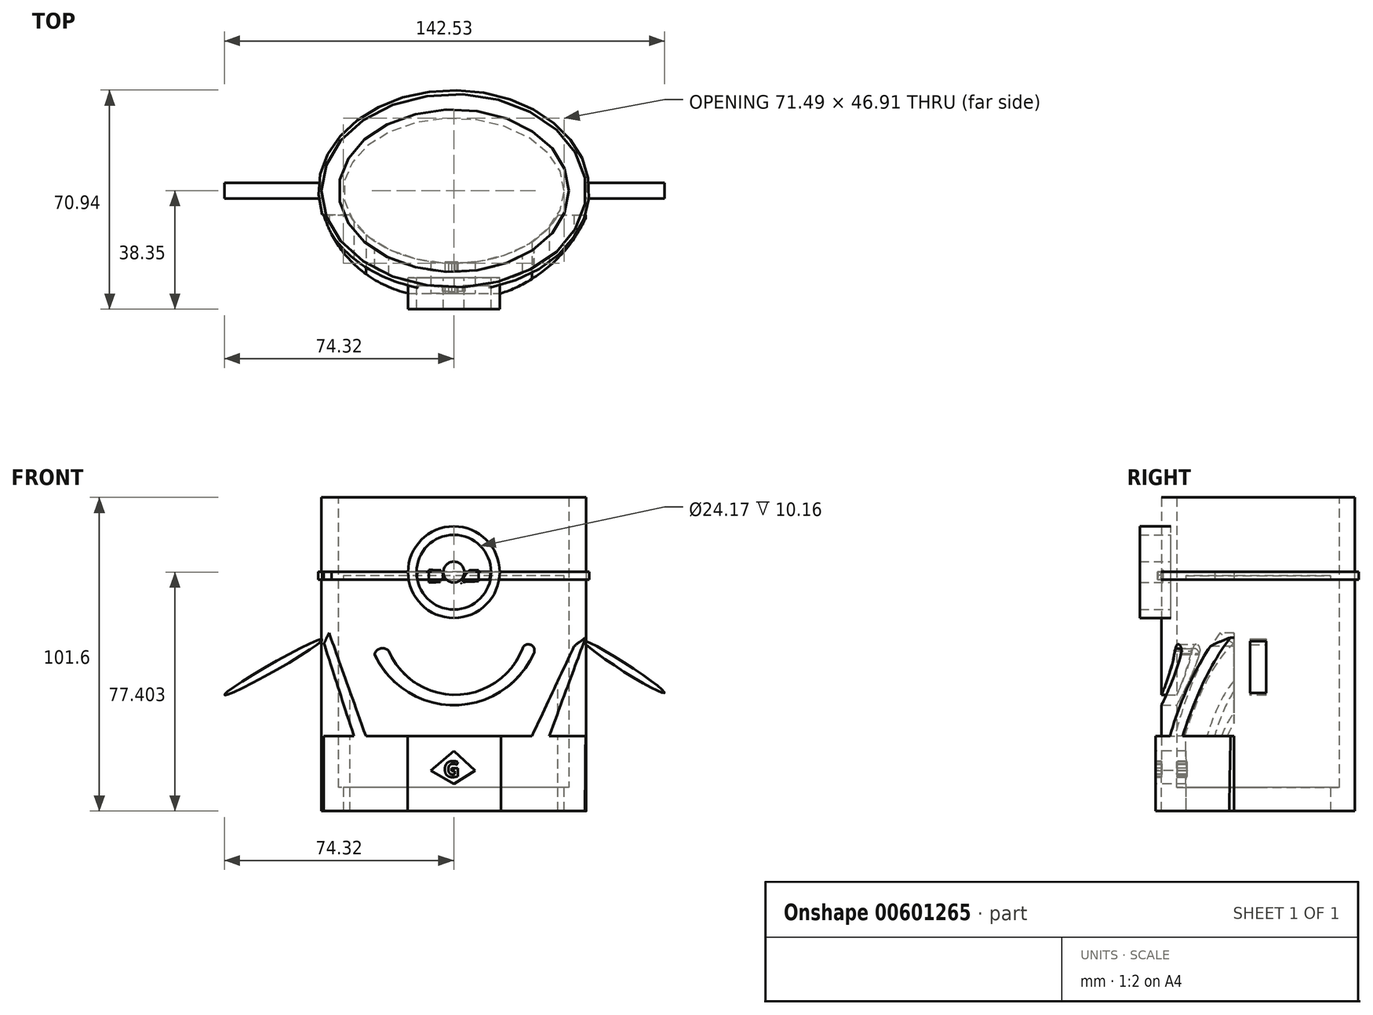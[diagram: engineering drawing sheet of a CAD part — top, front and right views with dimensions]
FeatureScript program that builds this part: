
annotation { "Feature Type Name" : "Feature", "Feature Type Description" : "" }
export const myFeature = defineFeature(function(context is Context, id is Id, definition is map)
    precondition{}
    {
        {
            var Q0;
            Q0=qCreatedBy(makeId("Top.planeOp"),FACE);
            var sketch = newSketch(context, id + "F0", { "sketchPlane" : qUnion([Q0])});
            skEllipse(sketch, "E0", {"center": v(0, 0) * mm, "majorRadius": 42.87 * mm, "minorRadius": 31.3 * mm, "majorAxis": v(-1, 0)});
            skEllipse(sketch, "E1", {"center": v(0, 0) * mm, "majorRadius": 37.27 * mm, "minorRadius": 26.31 * mm, "majorAxis": v(1, 0)});
            skSolve(sketch);
        }
        {
            var Q0;
            Q0=makeQuery(id+"F0.imprint","IMPRINT",FACE,{"disambiguationData":[TD([[makeQuery(id+"F0.imprint","IMPRINT",EDGE,{"derivedFrom":sQuery(id+"F0.wireOp",EDGE,"E0")}),1.0]])]});
            extrude(context, id + "F1", {"entities" : qUnion([Q0]), "depth" : 101.6 * mm, "offsetDistance" : 25.4 * mm});
        }
        {
            var Q0;
            Q0=qCreatedBy(makeId("Front.planeOp"),FACE);
            cPlane(context, id + "F2", {"entities" : qUnion([Q0]), "cplaneType" : CPlaneType.OFFSET, "offset" : 28.2 * mm, "width" : 152.4 * mm, "height" : 152.4 * mm});
        }
        {
            var Q0;
            Q0=qCreatedBy(id+"F2.planeOp",FACE);
            var sketch = newSketch(context, id + "F3", { "sketchPlane" : qUnion([Q0])});
            skCircle(sketch, "E2", {"center": v(0, 77.4) * mm, "radius": 14.84 * mm});
            skCircle(sketch, "E3", {"center": v(0, 77.4) * mm, "radius": 12.08 * mm});
            skCircle(sketch, "E4", {"center": v(0, 77.4) * mm, "radius": 3.38 * mm});
            skSolve(sketch);
        }
        {
            var Q0;
            Q0=makeQuery(id+"F3.imprint","IMPRINT",FACE,{"disambiguationData":[TD([[makeQuery(id+"F3.imprint","IMPRINT",EDGE,{"derivedFrom":sQuery(id+"F3.wireOp",EDGE,"E2")}),1.0]])]});
            extrude(context, id + "F4", {"entities" : qUnion([Q0]), "depth" : 10.16 * mm, "offsetDistance" : 25.4 * mm});
        }
        {
            var Q0;
            Q0=makeQuery(id+"F3.imprint","IMPRINT",FACE,{"disambiguationData":[TD([[makeQuery(id+"F3.imprint","IMPRINT",EDGE,{"derivedFrom":sQuery(id+"F3.wireOp",EDGE,"E4")}),1.0]])]});
            extrude(context, id + "F5", {"entities" : qUnion([Q0]), "depth" : 10.16 * mm, "offsetDistance" : 25.4 * mm});
        }
        {
            var Q0;
            Q0=qCreatedBy(makeId("Top.planeOp"),FACE);
            cPlane(context, id + "F6", {"entities" : qUnion([Q0]), "cplaneType" : CPlaneType.OFFSET, "offset" : 76.2 * mm, "width" : 152.4 * mm, "height" : 152.4 * mm});
        }
        {
            var Q0;
            Q0=qCreatedBy(id+"F6.planeOp",FACE);
            var sketch = newSketch(context, id + "F7", { "sketchPlane" : qUnion([Q0])});
            skEllipse(sketch, "E5", {"center": v(0, 0) * mm, "majorRadius": 43.86 * mm, "minorRadius": 32.59 * mm, "majorAxis": v(-1, 0)});
            skFitSpline(sketch, "E6.0", {"points": [v(-42.3, 1.52) * mm, v(-42.36, 0) * mm, v(-42.3, -1.52) * mm, v(-42.1, -3.52) * mm, v(-41.6, -6) * mm, v(-40.62, -8.91) * mm, v(-39.26, -11.74) * mm, v(-37.52, -14.48) * mm, v(-35.42, -17.08) * mm, v(-33.37, -19.14) * mm, v(-31.56, -20.7) * mm, v(-30.12, -21.83) * mm, v(-28.6, -22.9) * mm, v(-26.49, -24.25) * mm, v(-23.7, -25.79) * mm, v(-20.12, -27.37) * mm, v(-16.36, -28.7) * mm, v(-12.44, -29.74) * mm, v(-8.4, -30.5) * mm, v(-4.93, -30.88) * mm, v(-2.12, -31.04) * mm, v(0, -31.07) * mm, v(2.12, -31.04) * mm, v(4.93, -30.88) * mm, v(8.4, -30.5) * mm, v(12.44, -29.74) * mm, v(16.36, -28.7) * mm, v(20.12, -27.37) * mm, v(23.7, -25.79) * mm, v(26.49, -24.25) * mm, v(28.6, -22.9) * mm, v(30.12, -21.83) * mm, v(31.56, -20.7) * mm, v(33.37, -19.14) * mm, v(35.42, -17.08) * mm, v(37.52, -14.48) * mm, v(39.26, -11.74) * mm, v(40.62, -8.91) * mm, v(41.6, -6) * mm, v(42.1, -3.52) * mm, v(42.3, -1.52) * mm, v(42.36, 0) * mm, v(42.3, 1.52) * mm, v(42.1, 3.52) * mm, v(41.6, 6) * mm, v(40.62, 8.91) * mm, v(39.26, 11.74) * mm, v(37.52, 14.48) * mm, v(35.42, 17.08) * mm, v(33.37, 19.14) * mm, v(31.56, 20.7) * mm, v(30.12, 21.83) * mm, v(28.6, 22.9) * mm, v(26.49, 24.25) * mm, v(23.7, 25.79) * mm, v(20.12, 27.37) * mm, v(16.36, 28.7) * mm, v(12.44, 29.74) * mm, v(8.4, 30.5) * mm, v(4.93, 30.88) * mm, v(2.12, 31.04) * mm, v(0, 31.07) * mm, v(-2.12, 31.04) * mm, v(-4.93, 30.88) * mm, v(-8.4, 30.5) * mm, v(-12.44, 29.74) * mm, v(-16.36, 28.7) * mm, v(-20.12, 27.37) * mm, v(-23.7, 25.79) * mm, v(-26.49, 24.25) * mm, v(-28.6, 22.9) * mm, v(-30.12, 21.83) * mm, v(-31.56, 20.7) * mm, v(-33.37, 19.14) * mm, v(-35.42, 17.08) * mm, v(-37.52, 14.48) * mm, v(-39.26, 11.74) * mm, v(-40.62, 8.91) * mm, v(-41.6, 6) * mm, v(-42.1, 3.52) * mm, v(-42.3, 1.52) * mm, v(-42.36, 0) * mm, v(-42.3, -1.52) * mm, v(-42.3, 1.52) * mm]});
            skSolve(sketch);
        }
        {
            var Q0;
            Q0=makeQuery(id+"F7.imprint","IMPRINT",FACE,{"disambiguationData":[TD([[makeQuery(id+"F7.imprint","IMPRINT",EDGE,{"derivedFrom":sQuery(id+"F7.wireOp",EDGE,"E5")}),1.0]])]});
            extrude(context, id + "F8", {"entities" : qUnion([Q0]), "endBound" : BoundingType.SYMMETRIC, "depth" : 2.54 * mm, "offsetDistance" : 25.4 * mm});
        }
        {
            var Q0;
            Q0=qCreatedBy(makeId("Top.planeOp"),FACE);
            var sketch = newSketch(context, id + "F9", { "sketchPlane" : qUnion([Q0])});
            skEllipse(sketch, "E7", {"center": v(0, 0) * mm, "majorRadius": 39.81 * mm, "minorRadius": 29.81 * mm, "majorAxis": v(1, 0)});
            skSolve(sketch);
        }
        {
            var Q0;
            Q0=makeQuery(id+"F9.imprint","IMPRINT",FACE,{"disambiguationData":[TD([[makeQuery(id+"F9.imprint","IMPRINT",EDGE,{"derivedFrom":sQuery(id+"F9.wireOp",EDGE,"E7")}),1.0]])]});
            var Q1;
            Q1=sQuery(id+"F9.wireOp",EDGE,"E7");
            extrude(context, id + "F10", {"entities" : qUnion([Q0]), "operationType" : NewBodyOperationType.ADD, "surfaceEntities" : qUnion([Q1]), "depth" : 7.62 * mm, "offsetDistance" : 25.4 * mm});
        }
        {
            var Q0;
            Q0=qCreatedBy(id+"F2.planeOp",FACE);
            var sketch = newSketch(context, id + "F11", { "sketchPlane" : qUnion([Q0])});
            skArc(sketch, "E8", {"start": v(-25.68, 50.76) * mm, "mid": v(0.23, 34.33) * mm, "end": v(25.9, 51.15) * mm});
            skArc(sketch, "E9", {"start": v(-21.06, 51.92) * mm, "mid": v(0.85, 37.67) * mm, "end": v(22.24, 52.68) * mm});
            skArc(sketch, "E10", {"start": v(-21.06, 51.92) * mm, "mid": v(-23.71, 52.7) * mm, "end": v(-25.68, 50.76) * mm});
            skArc(sketch, "E11", {"start": v(25.9, 51.15) * mm, "mid": v(24.9, 53.89) * mm, "end": v(22.24, 52.68) * mm});
            skSolve(sketch);
        }
        {
            var Q0;
            Q0=makeQuery(id+"F11.imprint","IMPRINT",FACE,{"disambiguationData":[TD([[makeQuery(id+"F11.imprint","IMPRINT",EDGE,{"derivedFrom":sQuery(id+"F11.wireOp",EDGE,"E8")}),1.0]])]});
            var Q1;
            Q1=sQuery(id+"F11.wireOp",EDGE,"E9");
            var Q2;
            Q2=sQuery(id+"F11.wireOp",EDGE,"E8");
            var Q3;
            Q3=sQuery(id+"F11.wireOp",EDGE,"E10");
            var Q4;
            Q4=sQuery(id+"F11.wireOp",EDGE,"E11");
            extrude(context, id + "F12", {"entities" : qUnion([Q0]), "operationType" : NewBodyOperationType.REMOVE, "surfaceEntities" : qUnion([Q1, Q2, Q3, Q4]), "endBound" : BoundingType.SYMMETRIC, "depth" : 25.4 * mm, "offsetDistance" : 25.4 * mm});
        }
        {
            var Q0;
            Q0=qCreatedBy(makeId("Front.planeOp"),FACE);
            var sketch = newSketch(context, id + "F13", { "sketchPlane" : qUnion([Q0])});
            skEllipse(sketch, "E12", {"center": v(-58.26, 46.72) * mm, "majorRadius": 18.47 * mm, "minorRadius": 1.24 * mm, "majorAxis": v(0.87, 0.5)});
            skEllipse(sketch, "E13", {"center": v(55.02, 46.72) * mm, "majorRadius": 15.64 * mm, "minorRadius": 1.25 * mm, "majorAxis": v(-0.84, 0.54)});
            skSolve(sketch);
        }
        {
            var Q0;
            Q0 = qSketchRegion(id + "F13", true);
            extrude(context, id + "F14", {"entities" : qUnion([Q0]), "operationType" : NewBodyOperationType.ADD, "endBound" : BoundingType.SYMMETRIC, "depth" : 5.08 * mm, "offsetDistance" : 25.4 * mm});
        }
        {
            var Q0;
            Q0=qCreatedBy(id+"F2.planeOp",FACE);
            cPlane(context, id + "F15", {"entities" : qUnion([Q0]), "cplaneType" : CPlaneType.OFFSET, "offset" : 5.08 * mm, "width" : 152.4 * mm, "height" : 152.4 * mm});
        }
        {
            var Q0;
            Q0=qCreatedBy(id+"F15.planeOp",FACE);
            var sketch = newSketch(context, id + "F16", { "sketchPlane" : qUnion([Q0])});
            skLineSegment(sketch, "E14", {"start": v(-28.48, 24.29) * mm, "end": v(25.3, 24.29) * mm});
            skLineSegment(sketch, "E15", {"start": v(25.3, 24.29) * mm, "end": v(38.93, 53.42) * mm});
            skLineSegment(sketch, "E16", {"start": v(38.93, 53.42) * mm, "end": v(42.65, 56.21) * mm});
            skLineSegment(sketch, "E17", {"start": v(42.65, 56.21) * mm, "end": v(30.88, 24.29) * mm});
            skLineSegment(sketch, "E18", {"start": v(30.88, 24.29) * mm, "end": v(42.65, 24.29) * mm});
            skLineSegment(sketch, "E19", {"start": v(42.65, 24.29) * mm, "end": v(30.88, 24.29) * mm});
            skLineSegment(sketch, "E20", {"start": v(-28.48, 24.29) * mm, "end": v(-40.41, 57.76) * mm});
            skLineSegment(sketch, "E21", {"start": v(-40.41, 57.76) * mm, "end": v(-42.05, 54.27) * mm});
            skLineSegment(sketch, "E22", {"start": v(-42.05, 54.27) * mm, "end": v(-32.35, 24.29) * mm});
            skLineSegment(sketch, "E23", {"start": v(-32.35, 24.29) * mm, "end": v(-43.2, 24.29) * mm});
            skLineSegment(sketch, "E24", {"start": v(-7.4, 13.13) * mm, "end": v(0, 19.48) * mm});
            skLineSegment(sketch, "E25", {"start": v(0, 19.48) * mm, "end": v(6.85, 13.13) * mm});
            skLineSegment(sketch, "E26", {"start": v(6.85, 13.13) * mm, "end": v(0, 8.79) * mm});
            skLineSegment(sketch, "E27", {"start": v(0, 8.79) * mm, "end": v(-7.4, 13.13) * mm});
            skLineSegment(sketch, "E28", {"start": v(-43.2, 24.29) * mm, "end": v(-42.23, 0) * mm});
            skLineSegment(sketch, "E29", {"start": v(-42.23, 0) * mm, "end": v(42.45, 0) * mm});
            skLineSegment(sketch, "E30", {"start": v(42.45, 0) * mm, "end": v(42.65, 24.29) * mm});
            skLineSegment(sketch, "E31.trimOffspring", {"start": v(25.3, 24.29) * mm, "end": v(-28.48, 24.29) * mm});
            skSolve(sketch);
        }
        {
            var Q0;
            Q0=makeQuery(id+"F16.imprint","IMPRINT",FACE,{"disambiguationData":[TD([[makeQuery(id+"F16.imprint","IMPRINT",EDGE,{"derivedFrom":sQuery(id+"F16.wireOp",EDGE,"E15")}),-1.0]])]});
            var Q1;
            Q1=makeQuery(id+"F1.opExtrude","SWEPT_FACE",FACE,{"disambiguationData":[OSD([sQuery(id+"F0.wireOp",EDGE,"E0")])]});
            extrude(context, id + "F17", {"entities" : qUnion([Q0]), "oppositeDirection" : true, "depth" : 25.4 * mm, "endBoundEntityFace" : qUnion([Q1]), "offsetDistance" : 25.4 * mm});
        }
        {
            var Q0;
            Q0=qCreatedBy(id+"F6.planeOp",FACE);
            var sketch = newSketch(context, id + "F18", { "sketchPlane" : qUnion([Q0])});
            skEllipse(sketch, "E32", {"center": v(0, 0) * mm, "majorRadius": 35.74 * mm, "minorRadius": 23.45 * mm, "majorAxis": v(1, 0)});
            skSolve(sketch);
        }
        {
            var Q0;
            Q0=makeQuery(id+"F18.imprint","IMPRINT",FACE,{"disambiguationData":[TD([[makeQuery(id+"F18.imprint","IMPRINT",EDGE,{"derivedFrom":sQuery(id+"F18.wireOp",EDGE,"E32")}),1.0]])]});
            var Q1;
            Q1=sQuery(id+"F18.wireOp",EDGE,"E32");
            extrude(context, id + "F19", {"entities" : qUnion([Q0]), "operationType" : NewBodyOperationType.REMOVE, "surfaceEntities" : qUnion([Q1]), "oppositeDirection" : true, "depth" : 76.2 * mm, "offsetDistance" : 25.4 * mm});
        }
        {
            var Q0;
            Q0=makeQuery(id+"F17.opExtrude","CAP_FACE",FACE,{"disambiguationData":[OSD([sQuery(id+"F16.wireOp",EDGE,"E15"),sQuery(id+"F16.wireOp",EDGE,"E16"),sQuery(id+"F16.wireOp",EDGE,"E17"),sQuery(id+"F16.wireOp",EDGE,"E19"),sQuery(id+"F16.wireOp",EDGE,"E20"),sQuery(id+"F16.wireOp",EDGE,"E21"),sQuery(id+"F16.wireOp",EDGE,"E22"),sQuery(id+"F16.wireOp",EDGE,"E23"),sQuery(id+"F16.wireOp",EDGE,"E24"),sQuery(id+"F16.wireOp",EDGE,"E25"),sQuery(id+"F16.wireOp",EDGE,"E26"),sQuery(id+"F16.wireOp",EDGE,"E27"),sQuery(id+"F16.wireOp",EDGE,"E28"),sQuery(id+"F16.wireOp",EDGE,"E29"),sQuery(id+"F16.wireOp",EDGE,"E30"),sQuery(id+"F16.wireOp",EDGE,"E31.trimOffspring")])],"isStart":true});
            var sketch = newSketch(context, id + "F20", { "sketchPlane" : qUnion([Q0])});
            skText(sketch, "E33", { "text": "G", "fontName": "OpenSans-Bold.ttf"});
            const initialGuessF20  = {"E33": [-0.00332, 0.01106, 1, 0, 0.00515]};
            skSetInitialGuess(sketch, initialGuessF20);
            skSolve(sketch);
        }
        {
            var Q0;
            Q0=makeQuery(id+"F20.imprint","IMPRINT",FACE,{"disambiguationData":[TD([[makeQuery(id+"F20.imprint","IMPRINT",EDGE,{"derivedFrom":sQuery(id+"F20.wireOp",EDGE,"E33.sketch_text.stroke-0")}),-1.0]])]});
            extrude(context, id + "F21", {"entities" : qUnion([Q0]), "operationType" : NewBodyOperationType.ADD, "oppositeDirection" : true, "depth" : 10.16 * mm, "offsetDistance" : 25.4 * mm});
        }
        {
            var Q0;
            Q0=qCreatedBy(id+"F15.planeOp",FACE);
            var sketch = newSketch(context, id + "F22", { "sketchPlane" : qUnion([Q0])});
            skLineSegment(sketch, "E34", {"start": v(-4.25, 78.4) * mm, "end": v(-2.49, 73.77) * mm});
            skLineSegment(sketch, "E35", {"start": v(-2.49, 73.77) * mm, "end": v(-11.02, 73.77) * mm});
            skLineSegment(sketch, "E36", {"start": v(-11.02, 73.77) * mm, "end": v(-11.67, 77.88) * mm});
            skLineSegment(sketch, "E37", {"start": v(-11.67, 77.88) * mm, "end": v(-4.25, 78.4) * mm});
            skLineSegment(sketch, "E38", {"start": v(2.4, 73.77) * mm, "end": v(3.96, 78.14) * mm});
            skLineSegment(sketch, "E39", {"start": v(3.96, 78.14) * mm, "end": v(11.65, 78.14) * mm});
            skLineSegment(sketch, "E40", {"start": v(11.65, 78.14) * mm, "end": v(11, 74.42) * mm});
            skLineSegment(sketch, "E41", {"start": v(11, 74.42) * mm, "end": v(2.4, 73.77) * mm});
            skSolve(sketch);
        }
        {
            var Q0;
            Q0=makeQuery(id+"F22.imprint","IMPRINT",FACE,{"disambiguationData":[TD([[makeQuery(id+"F22.imprint","IMPRINT",EDGE,{"derivedFrom":sQuery(id+"F22.wireOp",EDGE,"E38")}),-1.0]])]});
            var Q1;
            Q1=makeQuery(id+"F22.imprint","IMPRINT",FACE,{"disambiguationData":[TD([[makeQuery(id+"F22.imprint","IMPRINT",EDGE,{"derivedFrom":sQuery(id+"F22.wireOp",EDGE,"E34")}),-1.0]])]});
            extrude(context, id + "F23", {"entities" : qUnion([Q0, Q1]), "operationType" : NewBodyOperationType.REMOVE, "oppositeDirection" : true, "depth" : 2.03 * mm, "offsetDistance" : 25.4 * mm});
        }
        {
            var Q0;
            Q0=qCreatedBy(id+"F15.planeOp",FACE);
            var sketch = newSketch(context, id + "F24", { "sketchPlane" : qUnion([Q0])});
            skArc(sketch, "E42", {"start": v(-10.65, 78.14) * mm, "mid": v(-11.92, 76) * mm, "end": v(-10.32, 74.1) * mm});
            skArc(sketch, "E43", {"start": v(-4.41, 74.17) * mm, "mid": v(-3.48, 76.06) * mm, "end": v(-4.17, 78.06) * mm});
            skLineSegment(sketch, "E44", {"start": v(-10.65, 78.14) * mm, "end": v(-4.17, 78.06) * mm});
            skLineSegment(sketch, "E45", {"start": v(-10.32, 74.1) * mm, "end": v(-4.41, 74.17) * mm});
            skArc(sketch, "E46", {"start": v(5.21, 77.98) * mm, "mid": v(3.62, 76.4) * mm, "end": v(2.95, 74.25) * mm});
            skArc(sketch, "E47", {"start": v(11.12, 74.58) * mm, "mid": v(11.77, 76.21) * mm, "end": v(11.77, 77.98) * mm});
            skLineSegment(sketch, "E48", {"start": v(5.21, 77.98) * mm, "end": v(11.77, 77.98) * mm});
            skLineSegment(sketch, "E49", {"start": v(2.95, 74.25) * mm, "end": v(11.12, 74.58) * mm});
            skSolve(sketch);
        }
        {
            var Q0;
            Q0=makeQuery(id+"F24.imprint","IMPRINT",FACE,{"disambiguationData":[TD([[makeQuery(id+"F24.imprint","IMPRINT",EDGE,{"derivedFrom":sQuery(id+"F24.wireOp",EDGE,"E42")}),1.0]])]});
            var Q1;
            Q1=makeQuery(id+"F24.imprint","IMPRINT",FACE,{"disambiguationData":[TD([[makeQuery(id+"F24.imprint","IMPRINT",EDGE,{"derivedFrom":sQuery(id+"F24.wireOp",EDGE,"E46")}),1.0]])]});
            extrude(context, id + "F25", {"entities" : qUnion([Q0, Q1]), "operationType" : NewBodyOperationType.REMOVE, "oppositeDirection" : true, "depth" : 2.54 * mm, "offsetDistance" : 25.4 * mm});
        }
        {
            var Q0;
            Q0=makeQuery(id+"F10.boolean.opBoolean","MERGE",FACE,{"derivedFrom":[makeQuery(id+"F1.opExtrude","CAP_FACE",FACE,{"disambiguationData":[OSD([sQuery(id+"F0.wireOp",EDGE,"E0"),sQuery(id+"F0.wireOp",EDGE,"E1")])],"isStart":true}),makeQuery(id+"F10.opExtrude","CAP_FACE",FACE,{"disambiguationData":[OSD([sQuery(id+"F9.wireOp",EDGE,"E7")])],"isStart":true})]});
            var sketch = newSketch(context, id + "F26", { "sketchPlane" : qUnion([Q0])});
            skLineSegment(sketch, "E50", {"start": v(-15.52, 33.92) * mm, "end": v(-44.17, 33.92) * mm});
            skLineSegment(sketch, "E51", {"start": v(-44.17, 33.92) * mm, "end": v(-44.17, 7.76) * mm});
            skLineSegment(sketch, "E52", {"start": v(-44.17, 7.76) * mm, "end": v(-42.14, 7.76) * mm});
            skLineSegment(sketch, "E53", {"start": v(-15.52, 33.92) * mm, "end": v(-14.85, 33.19) * mm});
            skArc(sketch, "E54", {"start": v(-14.85, 33.19) * mm, "mid": v(-31.91, 24.14) * mm, "end": v(-42.14, 7.76) * mm});
            skSolve(sketch);
        }
        {
            var Q0;
            Q0=makeQuery(id+"F26.imprint","IMPRINT",FACE,{"disambiguationData":[TD([[makeQuery(id+"F26.imprint","IMPRINT",EDGE,{"derivedFrom":sQuery(id+"F26.wireOp",EDGE,"E50")}),1.0]])]});
            extrude(context, id + "F27", {"entities" : qUnion([Q0]), "operationType" : NewBodyOperationType.REMOVE, "oppositeDirection" : true, "depth" : 127 * mm, "offsetDistance" : 25.4 * mm});
        }
        {
            var Q0;
            Q0=makeQuery(id+"F10.boolean.opBoolean","MERGE",FACE,{"derivedFrom":[makeQuery(id+"F1.opExtrude","CAP_FACE",FACE,{"disambiguationData":[OSD([sQuery(id+"F0.wireOp",EDGE,"E0"),sQuery(id+"F0.wireOp",EDGE,"E1")])],"isStart":true}),makeQuery(id+"F10.opExtrude","CAP_FACE",FACE,{"disambiguationData":[OSD([sQuery(id+"F9.wireOp",EDGE,"E7")])],"isStart":true})]});
            var sketch = newSketch(context, id + "F28", { "sketchPlane" : qUnion([Q0])});
            skLineSegment(sketch, "E55", {"start": v(43.02, 8.14) * mm, "end": v(43.02, 34.04) * mm});
            skLineSegment(sketch, "E56", {"start": v(43.02, 34.04) * mm, "end": v(15.7, 34.04) * mm});
            skLineSegment(sketch, "E57", {"start": v(15.7, 34.04) * mm, "end": v(14.95, 33.38) * mm});
            skLineSegment(sketch, "E58", {"start": v(43.02, 8.14) * mm, "end": v(42.44, 7.87) * mm});
            skArc(sketch, "E59", {"start": v(43.02, 8.14) * mm, "mid": v(31.67, 23.75) * mm, "end": v(14.95, 33.38) * mm});
            skSolve(sketch);
        }
        {
            var Q0;
            Q0=makeQuery(id+"F28.imprint","IMPRINT",FACE,{"disambiguationData":[TD([[makeQuery(id+"F28.imprint","IMPRINT",EDGE,{"derivedFrom":sQuery(id+"F28.wireOp",EDGE,"E55")}),1.0]])]});
            extrude(context, id + "F29", {"entities" : qUnion([Q0]), "operationType" : NewBodyOperationType.REMOVE, "oppositeDirection" : true, "depth" : 127 * mm, "offsetDistance" : 25.4 * mm});
        }
    });
